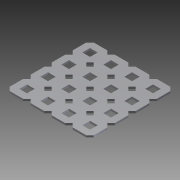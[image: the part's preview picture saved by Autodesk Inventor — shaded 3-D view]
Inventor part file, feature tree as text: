
AUTODESK INVENTOR PART (.ipt)
format: ipt  version: 2014 SP1 (Build 180222100, 222)  size: 560,640 bytes
history: native  units: in
note: dims shown in document units (in); Inventor stores cm internally (conversion verified against a paired STEP export)
features: other x1, imported_body x1, extrude x1, sketch x1
ambient origin geometry x8: Origin, YZ Plane, XZ Plane, XY Plane, X Axis, Y Axis, Z Axis, Center Point
bodies: Body1 (feature_tree)
feature tree (4):
  parser-record x1  (decoder bookkeeping rows leaked as tree rows — omitted from the tree; the rows remain in map.json)
  imported_body  "Base1"
  extrude  "Extrusion1"  Depth=1.0in TaperAngle=0.0deg
  sketch  "Sketch1"  dims[d0=2.0in d1=1.0in d2=0.0in d3=0.5in]
